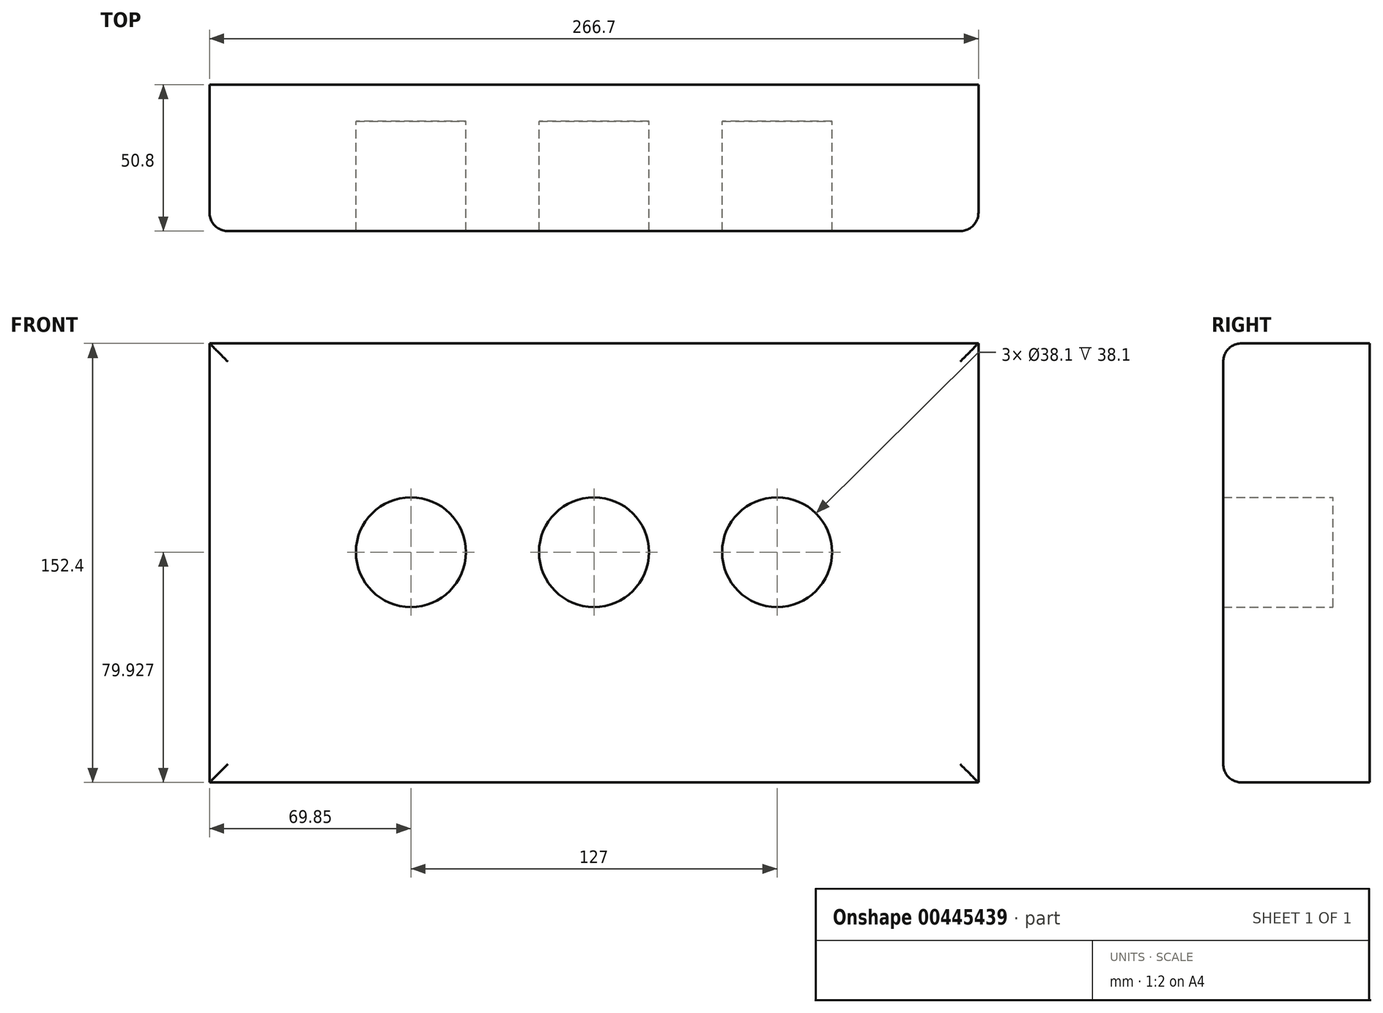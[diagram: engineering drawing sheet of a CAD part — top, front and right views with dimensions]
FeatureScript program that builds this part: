
annotation { "Feature Type Name" : "Feature", "Feature Type Description" : "" }
export const myFeature = defineFeature(function(context is Context, id is Id, definition is map)
    precondition{}
    {
        {
            var Q0;
            Q0=qCreatedBy(makeId("Front.planeOp"),FACE);
            var sketch = newSketch(context, id + "F0", { "sketchPlane" : qUnion([Q0])});
            skLineSegment(sketch, "E0.bottom", {"start": v(133.35, 76.2) * mm, "end": v(-133.35, 76.2) * mm});
            skLineSegment(sketch, "E0.top", {"start": v(133.35, -76.2) * mm, "end": v(-133.35, -76.2) * mm});
            skLineSegment(sketch, "E0.left", {"start": v(133.35, 76.2) * mm, "end": v(133.35, -76.2) * mm});
            skLineSegment(sketch, "E0.right", {"start": v(-133.35, 76.2) * mm, "end": v(-133.35, -76.2) * mm});
            skPoint(sketch, "E0.middle", {"position": v(0, 0) * mm});
            skCircle(sketch, "E1", {"center": v(0, 3.73) * mm, "radius": 19.05 * mm});
            skLineSegment(sketch, "E2", {"start": v(-19.05, 3.73) * mm, "end": v(-63.5, 3.73) * mm});
            skCircle(sketch, "E3", {"center": v(-63.5, 3.73) * mm, "radius": 19.05 * mm});
            skLineSegment(sketch, "E4", {"start": v(19.05, 3.73) * mm, "end": v(63.5, 3.73) * mm});
            skCircle(sketch, "E5", {"center": v(63.5, 3.73) * mm, "radius": 19.05 * mm});
            skSolve(sketch);
        }
        {
            var Q0;
            Q0 = qSketchRegion(id + "F0", true);
            extrude(context, id + "F1", {"entities" : qUnion([Q0]), "depth" : 50.8 * mm});
        }
        {
            var Q0;
            Q0=makeQuery(id+"F0.imprint","IMPRINT",FACE,{"disambiguationData":[TD([[makeQuery(id+"F0.imprint","IMPRINT",EDGE,{"derivedFrom":sQuery(id+"F0.wireOp",EDGE,"E3")}),1.0]])]});
            var Q1;
            {var subQ0=sQuery(id+"F0.wireOp",EDGE,"E1");var subQ1=makeQuery(id+"F0.imprint","IMPRINT",VERTEX,{"disambiguationData":[OD(0.0)],"derivedFrom":subQ0});Q1=makeQuery(id+"F0.imprint","IMPRINT",FACE,{"disambiguationData":[TD([[makeQuery(id+"F0.imprint","IMPRINT",EDGE,{"disambiguationData":[TD([[subQ1,1.0]])],"derivedFrom":subQ0}),1.0]])]});}
            var Q2;
            Q2=makeQuery(id+"F0.imprint","IMPRINT",FACE,{"disambiguationData":[TD([[makeQuery(id+"F0.imprint","IMPRINT",EDGE,{"derivedFrom":sQuery(id+"F0.wireOp",EDGE,"E5")}),1.0]])]});
            extrude(context, id + "F2", {"entities" : qUnion([Q0, Q1, Q2]), "operationType" : NewBodyOperationType.ADD, "depth" : 12.7 * mm});
        }
        {
            var Q0;
            Q0=makeQuery(id+"F1.opExtrude","CAP_EDGE",EDGE,{"disambiguationData":[OSD([sQuery(id+"F0.wireOp",EDGE,"E0.right")])],"isStart":false});
            var Q1;
            Q1=makeQuery(id+"F1.opExtrude","CAP_EDGE",EDGE,{"disambiguationData":[OSD([sQuery(id+"F0.wireOp",EDGE,"E0.top")])],"isStart":false});
            var Q2;
            Q2=makeQuery(id+"F1.opExtrude","CAP_EDGE",EDGE,{"disambiguationData":[OSD([sQuery(id+"F0.wireOp",EDGE,"E0.left")])],"isStart":false});
            var Q3;
            Q3=makeQuery(id+"F1.opExtrude","CAP_EDGE",EDGE,{"disambiguationData":[OSD([sQuery(id+"F0.wireOp",EDGE,"E0.bottom")])],"isStart":false});
            fillet(context, id + "F3", {"entities" : qUnion([Q0, Q1, Q2, Q3]), "radius" : 6.35 * mm, "tangentPropagation" : true, "allowEdgeOverflow" : false});
        }
    });
